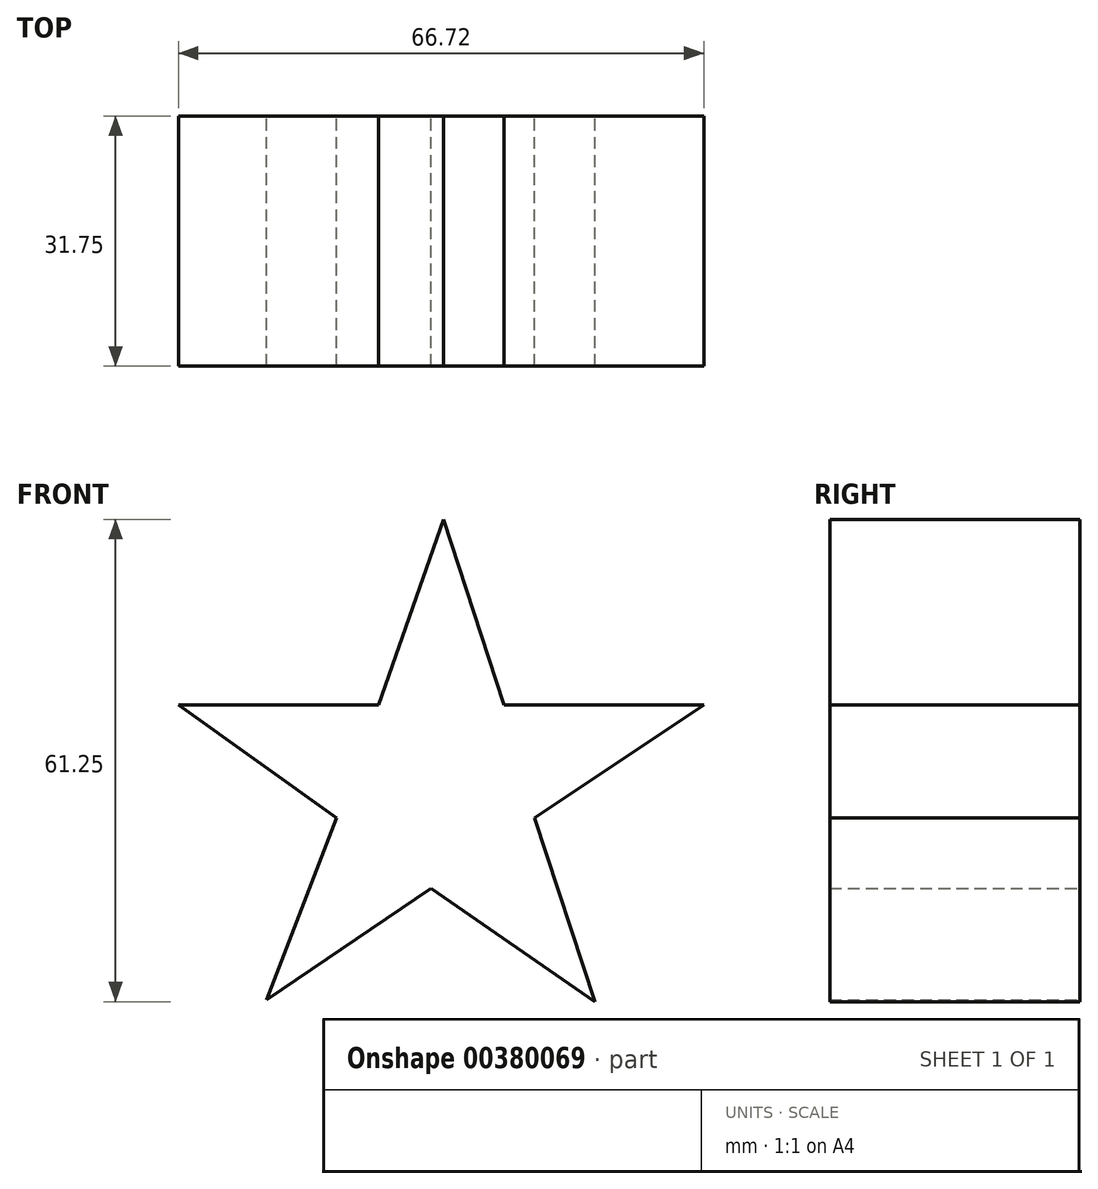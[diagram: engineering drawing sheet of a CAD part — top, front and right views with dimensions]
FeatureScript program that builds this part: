
annotation { "Feature Type Name" : "Feature", "Feature Type Description" : "" }
export const myFeature = defineFeature(function(context is Context, id is Id, definition is map)
    precondition{}
    {
        {
            var Q0;
            Q0=qCreatedBy(makeId("Front.planeOp"),FACE);
            var sketch = newSketch(context, id + "F0", { "sketchPlane" : qUnion([Q0])});
            skLineSegment(sketch, "E0.bottom", {"start": v(-40.86, 24.63) * mm, "end": v(53.66, 24.63) * mm});
            skLineSegment(sketch, "E0.top", {"start": v(-40.86, -46.4) * mm, "end": v(53.66, -46.4) * mm});
            skLineSegment(sketch, "E0.left", {"start": v(-40.86, 24.63) * mm, "end": v(-40.86, -46.4) * mm});
            skLineSegment(sketch, "E0.right", {"start": v(53.66, 24.63) * mm, "end": v(53.66, -46.4) * mm});
            skSolve(sketch);
        }
        {
            var Q0;
            Q0 = qSketchRegion(id + "F0", true);
            extrude(context, id + "F1", {"entities" : qUnion([Q0]), "depth" : 25.4 * mm});
        }
        {
            var Q0;
            Q0=makeQuery(id+"F1.opExtrude","CAP_FACE",FACE,{"disambiguationData":[OSD([sQuery(id+"F0.wireOp",EDGE,"E0.bottom"),sQuery(id+"F0.wireOp",EDGE,"E0.top"),sQuery(id+"F0.wireOp",EDGE,"E0.left"),sQuery(id+"F0.wireOp",EDGE,"E0.right")])],"isStart":false});
            var sketch = newSketch(context, id + "F2", { "sketchPlane" : qUnion([Q0])});
            skLineSegment(sketch, "E1", {"start": v(-25.38, -3.55) * mm, "end": v(-5.3, -17.95) * mm});
            skLineSegment(sketch, "E2", {"start": v(-5.3, -17.95) * mm, "end": v(-14.23, -41.07) * mm});
            skLineSegment(sketch, "E3", {"start": v(-14.23, -41.07) * mm, "end": v(6.66, -26.87) * mm});
            skLineSegment(sketch, "E4", {"start": v(6.66, -26.87) * mm, "end": v(27.55, -41.27) * mm});
            skLineSegment(sketch, "E5", {"start": v(27.55, -41.27) * mm, "end": v(19.84, -17.95) * mm});
            skLineSegment(sketch, "E6", {"start": v(19.84, -17.95) * mm, "end": v(41.34, -3.55) * mm});
            skLineSegment(sketch, "E7", {"start": v(41.34, -3.55) * mm, "end": v(16, -3.55) * mm});
            skLineSegment(sketch, "E8", {"start": v(16, -3.55) * mm, "end": v(8.28, 19.98) * mm});
            skLineSegment(sketch, "E9", {"start": v(8.28, 19.98) * mm, "end": v(0, -3.55) * mm});
            skLineSegment(sketch, "E10", {"start": v(0, -3.55) * mm, "end": v(-25.38, -3.55) * mm});
            skSolve(sketch);
        }
        {
            var Q0;
            Q0 = qSketchRegion(id + "F2", true);
            extrude(context, id + "F3", {"entities" : qUnion([Q0]), "operationType" : NewBodyOperationType.ADD, "depth" : 6.35 * mm});
        }
        {
            var Q0;
            Q0=makeQuery(id+"F1.opExtrude","CAP_FACE",FACE,{"disambiguationData":[OSD([sQuery(id+"F0.wireOp",EDGE,"E0.bottom"),sQuery(id+"F0.wireOp",EDGE,"E0.top"),sQuery(id+"F0.wireOp",EDGE,"E0.left"),sQuery(id+"F0.wireOp",EDGE,"E0.right")])],"isStart":false});
            extrude(context, id + "F4", {"entities" : qUnion([Q0]), "operationType" : NewBodyOperationType.REMOVE, "oppositeDirection" : true, "depth" : 25.4 * mm});
        }
    });
